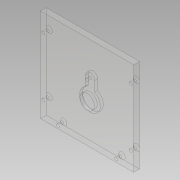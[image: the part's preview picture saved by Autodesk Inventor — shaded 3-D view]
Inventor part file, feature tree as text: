
AUTODESK INVENTOR PART (.ipt)
format: ipt  version: 2019 (Build 230136000, 136)  size: 131,584 bytes
history: native  units: mm
features: sketch x3, extrude x2, other x1, hole x1
ambient origin geometry x8: Origin, YZ Plane, XZ Plane, XY Plane, X Axis, Y Axis, Z Axis, Center Point
bodies: Body1 (feature_tree)
feature tree (7):
  other  "Sólido1"
  extrude  "Extrusión1"  Depth=160.0mm
  hole  "Agujero1"  [1 undecoded]
  extrude  "Extrusión2"  Depth=18.0mm
  sketch  "Boceto1"  dims[d0=160.0mm d1=160.0mm]
  sketch  "Boceto2"  dims[d2=25.0mm d3=14.988mm]
  sketch  "Boceto3"  dims[d4=5.0mm d5=18.0mm d6=10.0mm d7=0.0mm d9=5.5mm d10=6.0mm d11=11.0mm d12=2.0mm d13=90.0deg d14=20.0mm d15=20.594885mm d20=30.0mm d21=30.0mm d22=5.562258mm d23=5.29506mm d24=5.0mm d25=0.0mm d38=1.0mm d39=1.0mm d40=20.0mm d41=0.15mm d42=0.25mm d43=0.375mm d44=14.3117mm d45=20.0mm d46=20.594885mm d47=0.0625mm d48=0.75mm d49=0.375mm]
note: 1 required parameter value undecoded (feature->parameter linkage not recoverable at this tier; creation-order binding heuristic only, values carry confidence <= 0.55)
